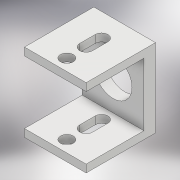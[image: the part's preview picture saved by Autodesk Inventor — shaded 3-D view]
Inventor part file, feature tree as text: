
AUTODESK INVENTOR PART (.ipt)
format: ipt  version: 2018.2 (Build 222227000, 227)  size: 153,600 bytes
history: native  units: mm
features: extrude x4, sketch x3
ambient origin geometry x8: Origin, YZ Plane, XZ Plane, XY Plane, X Axis, Y Axis, Z Axis, Center Point
bodies: Solid1 (feature_tree)
feature tree (7):
  sketch  "Sketch1"  dims[d0=9.8mm d1=2.0mm]
  extrude  "Extrusion1"  Depth=2.0mm
  extrude  "Extrusion2"  Depth=16.0mm
  extrude  "Extrusion3"  Depth=10.0mm
  extrude  "Extrusion4"  Depth=16.0mm
  sketch  "Sketch2"  dims[d2=16.0mm d3=8.0mm]
  sketch  "Sketch3"  dims[d4=0.15mm d5=0.15mm d6=16.0mm d7=2.0mm d8=2.0mm d9=3.0mm d10=0.0mm d11=15.0mm d12=0.0mm d13=3.3mm d14=3.0mm d15=7.0mm d16=0.0mm d17=3.3mm d18=4.0mm d19=5.0mm d20=10.0mm d21=0.0mm]
